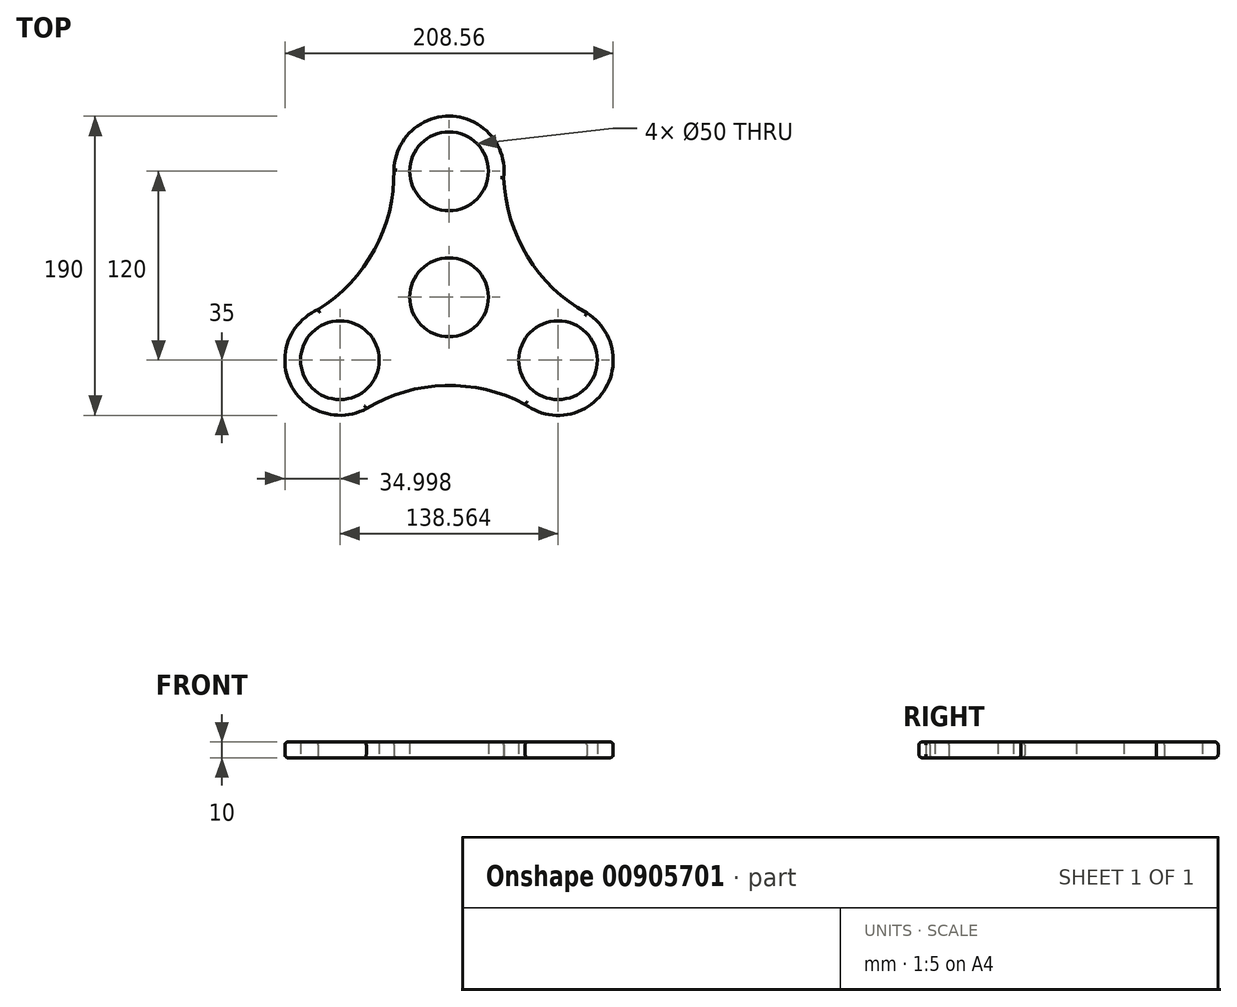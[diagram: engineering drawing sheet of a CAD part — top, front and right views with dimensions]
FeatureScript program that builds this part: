
annotation { "Feature Type Name" : "Feature", "Feature Type Description" : "" }
export const myFeature = defineFeature(function(context is Context, id is Id, definition is map)
    precondition{}
    {
        {
            var Q0;
            Q0=qCreatedBy(makeId("Top.planeOp"),FACE);
            var sketch = newSketch(context, id + "F0", { "sketchPlane" : qUnion([Q0])});
            skCircle(sketch, "E0", {"center": v(0, 0) * mm, "radius": 25 * mm});
            skCircle(sketch, "E1", {"center": v(0, 80) * mm, "radius": 25 * mm});
            skCircle(sketch, "E2.1.0", {"center": v(-69.28, -40) * mm, "radius": 25 * mm});
            skCircle(sketch, "E2.2.0", {"center": v(69.28, -40) * mm, "radius": 25 * mm});
            skCircle(sketch, "E3", {"center": v(0, 80) * mm, "radius": 35 * mm});
            skCircle(sketch, "E4.1.0", {"center": v(-69.28, -40) * mm, "radius": 35 * mm});
            skCircle(sketch, "E4.2.0", {"center": v(69.28, -40) * mm, "radius": 35 * mm});
            skLineSegment(sketch, "E5", {"start": v(0, 80) * mm, "end": v(69.28, -40) * mm, "construction": true});
            skLineSegment(sketch, "E6", {"start": v(29.62, 85.68) * mm, "end": v(98.08, -27.62) * mm, "construction": true});
            skArc(sketch, "E7", {"start": v(34.76, 75.93) * mm, "mid": v(49.77, 25.94) * mm, "end": v(87.51, -10.12) * mm});
            skArc(sketch, "E8.1.0", {"start": v(-83.14, -7.86) * mm, "mid": v(-47.35, 30.14) * mm, "end": v(-34.99, 80.85) * mm});
            skArc(sketch, "E8.2.0", {"start": v(48.37, -68.07) * mm, "mid": v(-2.42, -56.07) * mm, "end": v(-52.52, -70.73) * mm});
            skSolve(sketch);
        }
        {
            var Q0;
            Q0=makeQuery(id+"F0.imprint","IMPRINT",FACE,{"disambiguationData":[TD([[makeQuery(id+"F0.imprint","IMPRINT",EDGE,{"derivedFrom":sQuery(id+"F0.wireOp",EDGE,"E1")}),-1.0]])]});
            var Q1;
            Q1=makeQuery(id+"F0.imprint","IMPRINT",FACE,{"disambiguationData":[TD([[makeQuery(id+"F0.imprint","IMPRINT",EDGE,{"derivedFrom":sQuery(id+"F0.wireOp",EDGE,"E2.1.0")}),-1.0]])]});
            var Q2;
            Q2=makeQuery(id+"F0.imprint","IMPRINT",FACE,{"disambiguationData":[TD([[makeQuery(id+"F0.imprint","IMPRINT",EDGE,{"derivedFrom":sQuery(id+"F0.wireOp",EDGE,"E2.2.0")}),-1.0]])]});
            var Q3;
            Q3=makeQuery(id+"F0.imprint","IMPRINT",FACE,{"disambiguationData":[TD([[makeQuery(id+"F0.imprint","IMPRINT",EDGE,{"derivedFrom":sQuery(id+"F0.wireOp",EDGE,"E0")}),-1.0]])]});
            extrude(context, id + "F1", {"entities" : qUnion([Q0, Q1, Q2, Q3]), "depth" : 10 * mm, "offsetDistance" : 25 * mm});
        }
        {
            var Q0;
            Q0=makeQuery(id+"F1.opExtrude","CAP_EDGE",EDGE,{"disambiguationData":[OSD([sQuery(id+"F0.wireOp",EDGE,"E7")])],"isStart":true});
            var Q1;
            Q1=makeQuery(id+"F1.opExtrude","CAP_EDGE",EDGE,{"disambiguationData":[OSD([sQuery(id+"F0.wireOp",EDGE,"E3")])],"isStart":true});
            var Q2;
            Q2=makeQuery(id+"F1.opExtrude","CAP_EDGE",EDGE,{"disambiguationData":[OSD([sQuery(id+"F0.wireOp",EDGE,"E8.1.0")])],"isStart":true});
            var Q3;
            Q3=makeQuery(id+"F1.opExtrude","CAP_EDGE",EDGE,{"disambiguationData":[OSD([sQuery(id+"F0.wireOp",EDGE,"E4.1.0")])],"isStart":true});
            var Q4;
            Q4=makeQuery(id+"F1.opExtrude","CAP_EDGE",EDGE,{"disambiguationData":[OSD([sQuery(id+"F0.wireOp",EDGE,"E8.2.0")])],"isStart":true});
            var Q5;
            Q5=makeQuery(id+"F1.opExtrude","CAP_EDGE",EDGE,{"disambiguationData":[OSD([sQuery(id+"F0.wireOp",EDGE,"E4.2.0")])],"isStart":true});
            var Q6;
            Q6=makeQuery(id+"F1.opExtrude","CAP_EDGE",EDGE,{"disambiguationData":[OSD([sQuery(id+"F0.wireOp",EDGE,"E7")])],"isStart":false});
            var Q7;
            Q7=makeQuery(id+"F1.opExtrude","CAP_EDGE",EDGE,{"disambiguationData":[OSD([sQuery(id+"F0.wireOp",EDGE,"E3")])],"isStart":false});
            var Q8;
            Q8=makeQuery(id+"F1.opExtrude","CAP_EDGE",EDGE,{"disambiguationData":[OSD([sQuery(id+"F0.wireOp",EDGE,"E8.1.0")])],"isStart":false});
            var Q9;
            Q9=makeQuery(id+"F1.opExtrude","CAP_EDGE",EDGE,{"disambiguationData":[OSD([sQuery(id+"F0.wireOp",EDGE,"E4.1.0")])],"isStart":false});
            var Q10;
            Q10=makeQuery(id+"F1.opExtrude","CAP_EDGE",EDGE,{"disambiguationData":[OSD([sQuery(id+"F0.wireOp",EDGE,"E8.2.0")])],"isStart":false});
            var Q11;
            Q11=makeQuery(id+"F1.opExtrude","CAP_EDGE",EDGE,{"disambiguationData":[OSD([sQuery(id+"F0.wireOp",EDGE,"E4.2.0")])],"isStart":false});
            fillet(context, id + "F2", {"entities" : qUnion([Q0, Q1, Q2, Q3, Q4, Q5, Q6, Q7, Q8, Q9, Q10, Q11]), "radius" : 2 * mm, "tangentPropagation" : true, "allowEdgeOverflow" : false});
        }
    });
